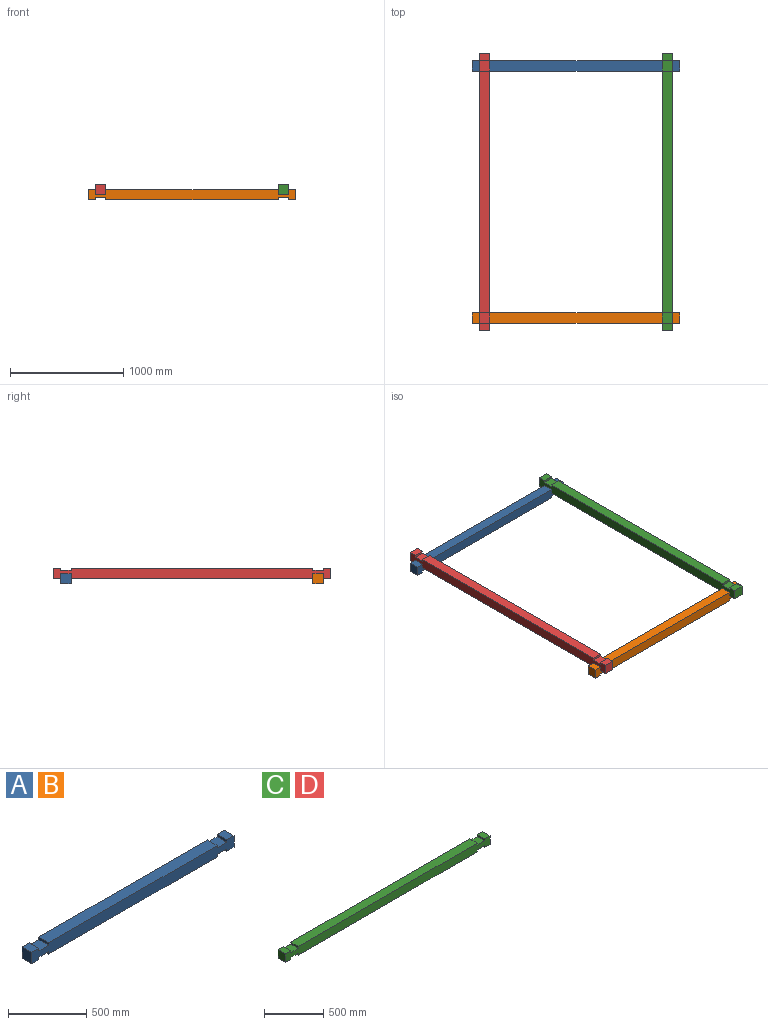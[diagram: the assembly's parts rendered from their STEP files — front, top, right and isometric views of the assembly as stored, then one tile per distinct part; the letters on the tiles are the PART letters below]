
ASSEMBLY  parts=4 mates=3
PART A: 22 faces, bbox 1828.8x88.9x88.9 mm
  f0: plane 88.9x63.5mm, normal (0,0,1), area 5645.1mm2, adj f4,f5,f8,f18
  f1: plane 1524x88.9mm, normal (0,0,1), area 135483.6mm2, adj f4,f5,f12,f16
  f2: plane 1524x88.9mm, normal (0,0,-1), area 135483.6mm2, adj f4,f5,f13,f20
  f3: plane 88.9x63.5mm, normal (0,0,-1), area 5645.1mm2, adj f4,f5,f8,f14
  f4: plane 1828.8x88.9mm, normal (0,-1,0), area 155806.1mm2, adj f0,f1,f2,f3,f6,f7,f8,f9
  f5: plane 1828.8x88.9mm, normal (0,1,0), area 155806.1mm2, adj f0,f1,f2,f3,f6,f7,f8,f9
  f6: plane 88.9x63.5mm, normal (0,0,1), area 5645.2mm2, adj f4,f5,f9,f10
  f7: plane 88.9x63.5mm, normal (0,0,-1), area 5645.2mm2, adj f4,f5,f9,f19
  f8: plane 88.9x88.9mm, normal (1,0,0), area 7903.2mm2, adj f0,f3,f4,f5
  f9: plane 88.9x88.9mm, normal (-1,0,0), area 7903.2mm2, adj f4,f5,f6,f7
  f10: plane 88.9x19.05mm, normal (1,0,0), area 1693.5mm2, adj f4,f5,f6,f11
  f11: plane 88.9x88.9mm, normal (0,0,1), area 7903.2mm2, adj f4,f5,f10,f12
  f12: plane 88.9x19.05mm, normal (-1,0,0), area 1693.5mm2, adj f1,f4,f5,f11
  f13: plane 88.9x19.05mm, normal (1,0,0), area 1693.5mm2, adj f2,f4,f5,f15
  f14: plane 88.9x19.05mm, normal (-1,0,0), area 1693.5mm2, adj f3,f4,f5,f15
  f15: plane 88.9x88.9mm, normal (0,0,-1), area 7903.2mm2, adj f4,f5,f13,f14
  f16: plane 88.9x19.05mm, normal (1,0,0), area 1693.5mm2, adj f1,f4,f5,f17
  f17: plane 88.9x88.9mm, normal (0,0,1), area 7903.2mm2, adj f4,f5,f16,f18
  f18: plane 88.9x19.05mm, normal (-1,0,0), area 1693.5mm2, adj f0,f4,f5,f17
  f19: plane 88.9x19.05mm, normal (1,0,0), area 1693.5mm2, adj f4,f5,f7,f21
  f20: plane 88.9x19.05mm, normal (-1,0,0), area 1693.5mm2, adj f2,f4,f5,f21
  f21: plane 88.9x88.9mm, normal (0,0,-1), area 7903.2mm2, adj f4,f5,f19,f20
PART B: same geometry as A
PART C: 22 faces, bbox 2438.4x88.9x88.9 mm
  f0: plane 88.9x63.5mm, normal (0,0,1), area 5645.2mm2, adj f4,f5,f8,f18
  f1: plane 2133.6x88.9mm, normal (0,0,1), area 189677mm2, adj f4,f5,f12,f16
  f2: plane 2133.6x88.9mm, normal (0,0,-1), area 189677mm2, adj f4,f5,f13,f20
  f3: plane 88.9x63.5mm, normal (0,0,-1), area 5645.2mm2, adj f4,f5,f8,f14
  f4: plane 2438.4x88.9mm, normal (0,-1,0), area 209999.6mm2, adj f0,f1,f2,f3,f6,f7,f8,f9
  f5: plane 2438.4x88.9mm, normal (0,1,0), area 209999.6mm2, adj f0,f1,f2,f3,f6,f7,f8,f9
  f6: plane 88.9x63.5mm, normal (0,0,1), area 5645.2mm2, adj f4,f5,f9,f10
  f7: plane 88.9x63.5mm, normal (0,0,-1), area 5645.2mm2, adj f4,f5,f9,f19
  f8: plane 88.9x88.9mm, normal (1,0,0), area 7903.2mm2, adj f0,f3,f4,f5
  f9: plane 88.9x88.9mm, normal (-1,0,0), area 7903.2mm2, adj f4,f5,f6,f7
  f10: plane 88.9x19.05mm, normal (1,0,0), area 1693.5mm2, adj f4,f5,f6,f11
  f11: plane 88.9x88.9mm, normal (0,0,1), area 7903.2mm2, adj f4,f5,f10,f12
  f12: plane 88.9x19.05mm, normal (-1,0,0), area 1693.5mm2, adj f1,f4,f5,f11
  f13: plane 88.9x19.05mm, normal (1,0,0), area 1693.5mm2, adj f2,f4,f5,f15
  f14: plane 88.9x19.05mm, normal (-1,0,0), area 1693.5mm2, adj f3,f4,f5,f15
  f15: plane 88.9x88.9mm, normal (0,0,-1), area 7903.2mm2, adj f4,f5,f13,f14
  f16: plane 88.9x19.05mm, normal (1,0,0), area 1693.5mm2, adj f1,f4,f5,f17
  f17: plane 88.9x88.9mm, normal (0,0,1), area 7903.2mm2, adj f4,f5,f16,f18
  f18: plane 88.9x19.05mm, normal (-1,0,0), area 1693.5mm2, adj f0,f4,f5,f17
  f19: plane 88.9x19.05mm, normal (1,0,0), area 1693.5mm2, adj f4,f5,f7,f21
  f20: plane 88.9x19.05mm, normal (-1,0,0), area 1693.5mm2, adj f2,f4,f5,f21
  f21: plane 88.9x88.9mm, normal (0,0,-1), area 7903.2mm2, adj f4,f5,f19,f20
PART D: same geometry as C
PLACE A t=(-4262.14,857.51,583.18)mm fixed
PLACE B t=(-4262.14,-1364.99,583.18)mm
PLACE C rot(axis=(0,0,-1),90deg) t=(-2585.74,1009.91,633.98)mm
PLACE D rot(axis=(0,0,-1),90deg) t=(-4198.64,1009.91,633.98)mm
MATE fastened A.f17 <-> C.f21  axis (0,0,1) through (-2541.29,901.96,564.13)mm
MATE fastened A.f11 <-> D.f21  axis (0,0,1) through (-4154.19,901.96,564.13)mm
MATE fastened B.f11 <-> D.f15  axis (0,0,1) through (-4154.19,-1320.54,564.13)mm
